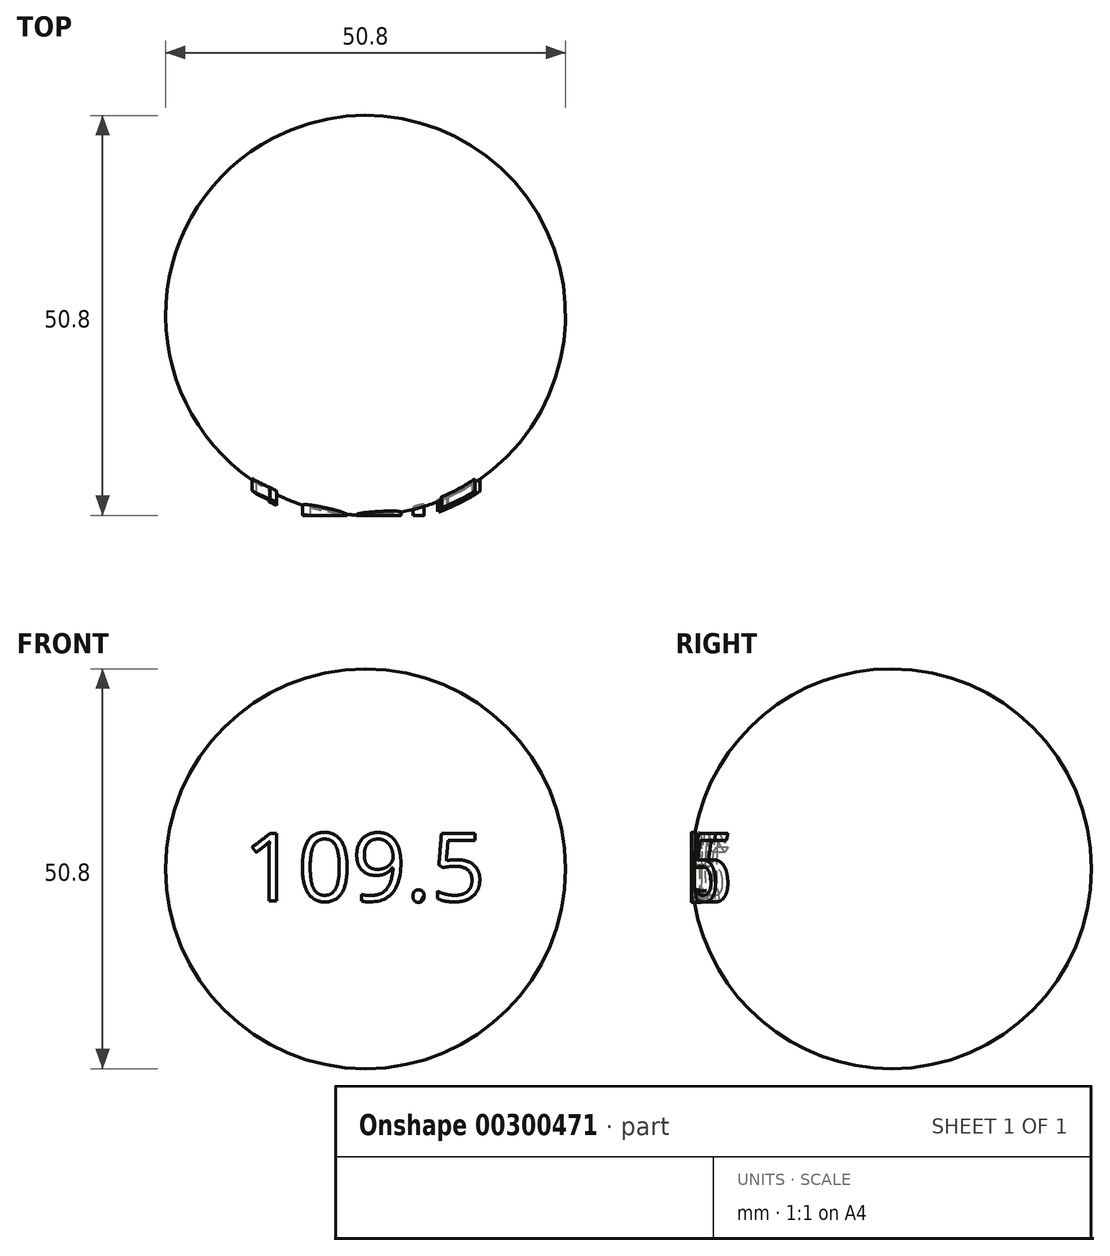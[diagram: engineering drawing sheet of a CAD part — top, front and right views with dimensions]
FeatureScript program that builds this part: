
annotation { "Feature Type Name" : "Feature", "Feature Type Description" : "" }
export const myFeature = defineFeature(function(context is Context, id is Id, definition is map)
    precondition{}
    {
        {
            var Q0;
            Q0=qCreatedBy(makeId("Front.planeOp"),FACE);
            var sketch = newSketch(context, id + "F0", { "sketchPlane" : qUnion([Q0])});
            skArc(sketch, "E0", {"start": v(0, 25.4) * mm, "mid": v(-25.4, 0) * mm, "end": v(0, -25.4) * mm});
            skLineSegment(sketch, "E1", {"start": v(0, 25.4) * mm, "end": v(0, -25.4) * mm});
            skSolve(sketch);
        }
        {
            var Q0;
            Q0=makeQuery(id+"F0.imprint","IMPRINT",FACE,{"disambiguationData":[TD([[makeQuery(id+"F0.imprint","IMPRINT",EDGE,{"derivedFrom":sQuery(id+"F0.wireOp",EDGE,"E0")}),1.0]])]});
            var Q1;
            Q1=sQuery(id+"F0.wireOp",EDGE,"E1");
            revolve(context, id + "F1", {"entities" : qUnion([Q0]), "axis" : qUnion([Q1]), "revolveType" : RevolveType.FULL});
        }
        {
            var Q0;
            Q0=qCreatedBy(makeId("Front.planeOp"),FACE);
            cPlane(context, id + "F2", {"entities" : qUnion([Q0]), "cplaneType" : CPlaneType.OFFSET, "offset" : 25.4 * mm, "width" : 152.4 * mm, "height" : 152.4 * mm});
        }
        {
            var Q0;
            Q0=qCreatedBy(id+"F2.planeOp",FACE);
            var sketch = newSketch(context, id + "F3", { "sketchPlane" : qUnion([Q0])});
            skText(sketch, "E2", { "text": "109.5", "fontName": "OpenSans-Regular.ttf"});
            const initialGuessF3  = {"E2": [-0.0155, -0.0041, 1, 0, 0.00866]};
            skSetInitialGuess(sketch, initialGuessF3);
            skSolve(sketch);
        }
        {
            var Q0;
            Q0 = qSketchRegion(id + "F3", true);
            extrude(context, id + "F4", {"entities" : qUnion([Q0]), "operationType" : NewBodyOperationType.ADD, "oppositeDirection" : true, "depth" : 6.35 * mm});
        }
        {
            var Q0;
            Q0=qCreatedBy(makeId("Right.planeOp"),FACE);
            var sketch = newSketch(context, id + "F5", { "sketchPlane" : qUnion([Q0])});
            skLineSegment(sketch, "E3", {"start": v(0, 0) * mm, "end": v(0, 43.7) * mm, "construction": true});
            skArc(sketch, "E4", {"start": v(0, 26.67) * mm, "mid": v(-26.67, 0) * mm, "end": v(0, -26.67) * mm});
            skArc(sketch, "E5", {"start": v(0, 33.57) * mm, "mid": v(-33.57, 0) * mm, "end": v(0, -33.57) * mm});
            skLineSegment(sketch, "E6", {"start": v(0, 33.57) * mm, "end": v(0, 26.67) * mm});
            skLineSegment(sketch, "E7", {"start": v(0, -26.67) * mm, "end": v(0, -33.57) * mm});
            skSolve(sketch);
        }
        {
            var Q0;
            Q0=makeQuery(id+"F5.imprint","IMPRINT",FACE,{"disambiguationData":[TD([[makeQuery(id+"F5.imprint","IMPRINT",EDGE,{"derivedFrom":sQuery(id+"F5.wireOp",EDGE,"E4")}),-1.0]])]});
            var Q1;
            Q1=sQuery(id+"F5.wireOp",EDGE,"E3");
            revolve(context, id + "F6", {"operationType" : NewBodyOperationType.REMOVE, "entities" : qUnion([Q0]), "axis" : qUnion([Q1]), "revolveType" : RevolveType.FULL, "oppositeDirection" : true});
        }
    });
